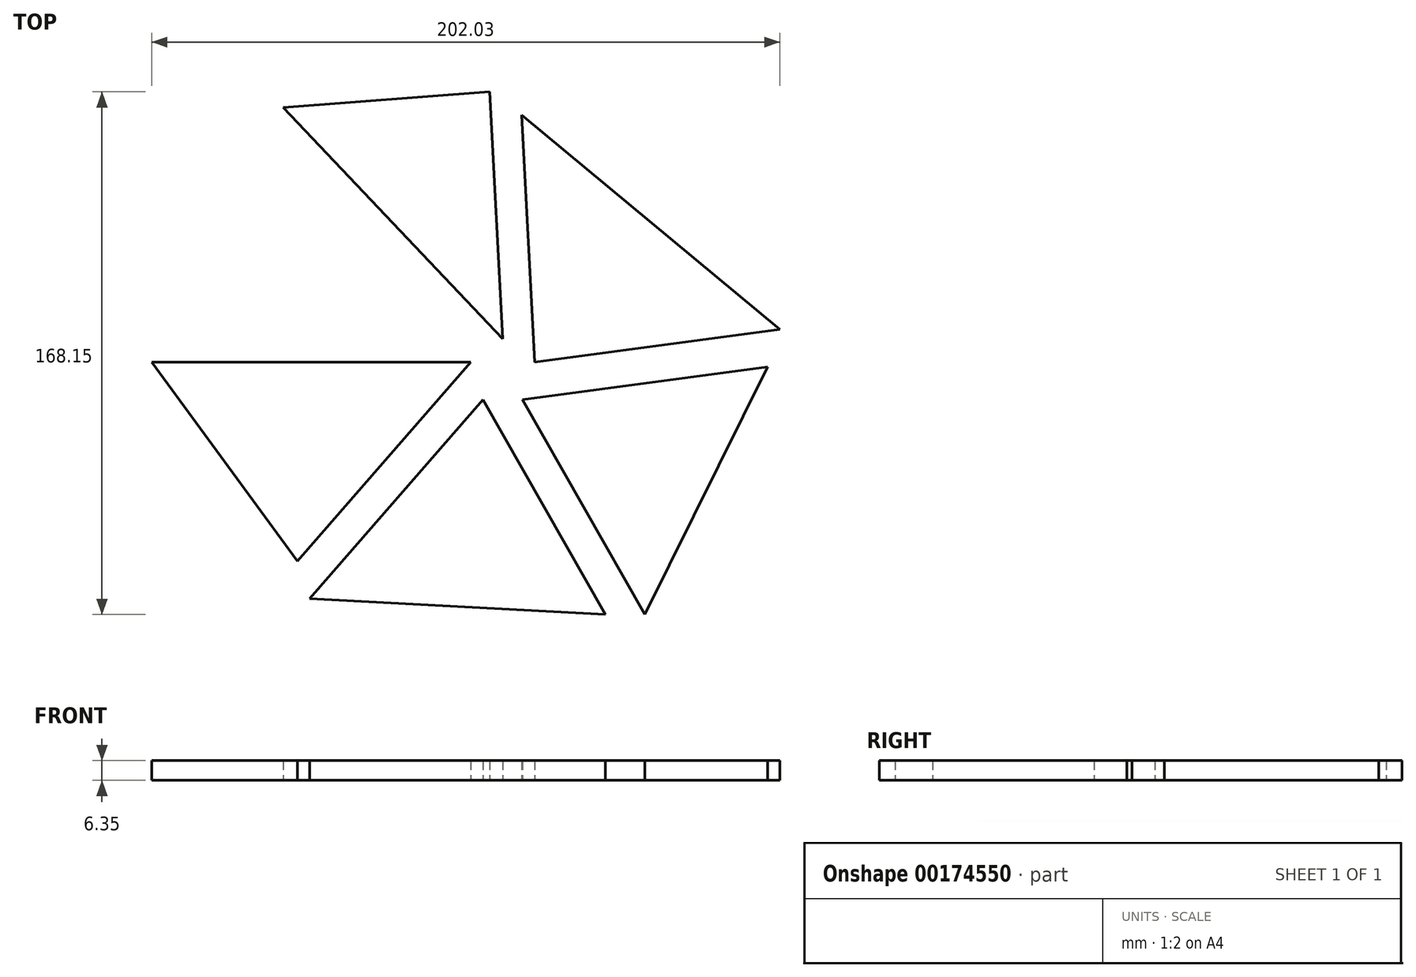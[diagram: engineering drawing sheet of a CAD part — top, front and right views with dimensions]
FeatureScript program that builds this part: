
annotation { "Feature Type Name" : "Feature", "Feature Type Description" : "" }
export const myFeature = defineFeature(function(context is Context, id is Id, definition is map)
    precondition{}
    {
        {
            var Q0;
            Q0=qCreatedBy(makeId("Top.planeOp"),FACE);
            var sketch = newSketch(context, id + "F0", { "sketchPlane" : qUnion([Q0])});
            skLineSegment(sketch, "E0", {"start": v(6.1, 86.9) * mm, "end": v(-60.4, 81.86) * mm});
            skLineSegment(sketch, "E1", {"start": v(-60.4, 81.86) * mm, "end": v(10.27, 7.46) * mm});
            skLineSegment(sketch, "E2", {"start": v(10.27, 7.46) * mm, "end": v(6.1, 86.9) * mm});
            skLineSegment(sketch, "E3", {"start": v(16.38, 79.44) * mm, "end": v(20.55, 0) * mm});
            skLineSegment(sketch, "E4", {"start": v(20.55, 0) * mm, "end": v(99.41, 10.46) * mm});
            skLineSegment(sketch, "E5", {"start": v(99.41, 10.46) * mm, "end": v(16.38, 79.44) * mm});
            skLineSegment(sketch, "E6", {"start": v(95.49, -1.62) * mm, "end": v(16.62, -12.08) * mm});
            skLineSegment(sketch, "E7", {"start": v(16.62, -12.08) * mm, "end": v(55.94, -81.24) * mm});
            skLineSegment(sketch, "E8", {"start": v(55.94, -81.24) * mm, "end": v(95.49, -1.62) * mm});
            skLineSegment(sketch, "E9", {"start": v(3.92, -12.08) * mm, "end": v(43.24, -81.24) * mm});
            skLineSegment(sketch, "E10", {"start": v(43.24, -81.24) * mm, "end": v(-51.88, -76.18) * mm});
            skLineSegment(sketch, "E11", {"start": v(-51.88, -76.18) * mm, "end": v(3.92, -12.08) * mm});
            skLineSegment(sketch, "E12", {"start": v(0, 0) * mm, "end": v(-102.62, 0) * mm});
            skLineSegment(sketch, "E13", {"start": v(-102.62, 0) * mm, "end": v(-55.8, -64.1) * mm});
            skLineSegment(sketch, "E14", {"start": v(-55.8, -64.1) * mm, "end": v(0, 0) * mm});
            skLineSegment(sketch, "E15", {"start": v(10.27, 7.46) * mm, "end": v(0, 0) * mm, "construction": true});
            skLineSegment(sketch, "E16", {"start": v(3.92, -12.08) * mm, "end": v(0, 0) * mm, "construction": true});
            skLineSegment(sketch, "E17", {"start": v(16.62, -12.08) * mm, "end": v(3.92, -12.08) * mm, "construction": true});
            skLineSegment(sketch, "E18", {"start": v(16.62, -12.08) * mm, "end": v(20.55, 0) * mm, "construction": true});
            skLineSegment(sketch, "E19", {"start": v(20.55, 0) * mm, "end": v(10.27, 7.46) * mm, "construction": true});
            skLineSegment(sketch, "E20", {"start": v(-60.4, 81.86) * mm, "end": v(-102.62, 0) * mm, "construction": true});
            skSolve(sketch);
        }
        {
            var Q0;
            Q0=qCreatedBy(makeId("Top.planeOp"),FACE);
            var sketch = newSketch(context, id + "F1", { "sketchPlane" : qUnion([Q0])});
            skLineSegment(sketch, "E21.1", {"start": v(6.1, 86.9) * mm, "end": v(-60.4, 81.86) * mm});
            skLineSegment(sketch, "E21.2", {"start": v(-102.62, 0) * mm, "end": v(-55.8, -64.1) * mm});
            skLineSegment(sketch, "E21.3", {"start": v(-55.8, -64.1) * mm, "end": v(0, 0) * mm});
            skLineSegment(sketch, "E21.5", {"start": v(-60.4, 81.86) * mm, "end": v(10.27, 7.46) * mm});
            skLineSegment(sketch, "E21.6", {"start": v(95.49, -1.62) * mm, "end": v(16.62, -12.08) * mm});
            skLineSegment(sketch, "E21.7", {"start": v(10.27, 7.46) * mm, "end": v(6.1, 86.9) * mm});
            skLineSegment(sketch, "E21.8", {"start": v(99.41, 10.46) * mm, "end": v(16.38, 79.44) * mm});
            skLineSegment(sketch, "E21.9", {"start": v(20.55, 0) * mm, "end": v(99.41, 10.46) * mm});
            skLineSegment(sketch, "E21.10", {"start": v(16.38, 79.44) * mm, "end": v(20.55, 0) * mm});
            skLineSegment(sketch, "E21.11", {"start": v(16.62, -12.08) * mm, "end": v(55.94, -81.24) * mm});
            skLineSegment(sketch, "E21.12", {"start": v(-51.88, -76.18) * mm, "end": v(3.92, -12.08) * mm});
            skLineSegment(sketch, "E21.13", {"start": v(55.94, -81.24) * mm, "end": v(95.49, -1.62) * mm});
            skLineSegment(sketch, "E21.15", {"start": v(0, 0) * mm, "end": v(-102.62, 0) * mm});
            skLineSegment(sketch, "E21.17", {"start": v(3.92, -12.08) * mm, "end": v(43.24, -81.24) * mm});
            skLineSegment(sketch, "E21.18", {"start": v(43.24, -81.24) * mm, "end": v(-51.88, -76.18) * mm});
            skSolve(sketch);
        }
        {
            var Q0;
            Q0 = qSketchRegion(id + "F1", true);
            extrude(context, id + "F2", {"entities" : qUnion([Q0]), "depth" : 6.35 * mm});
        }
    });
